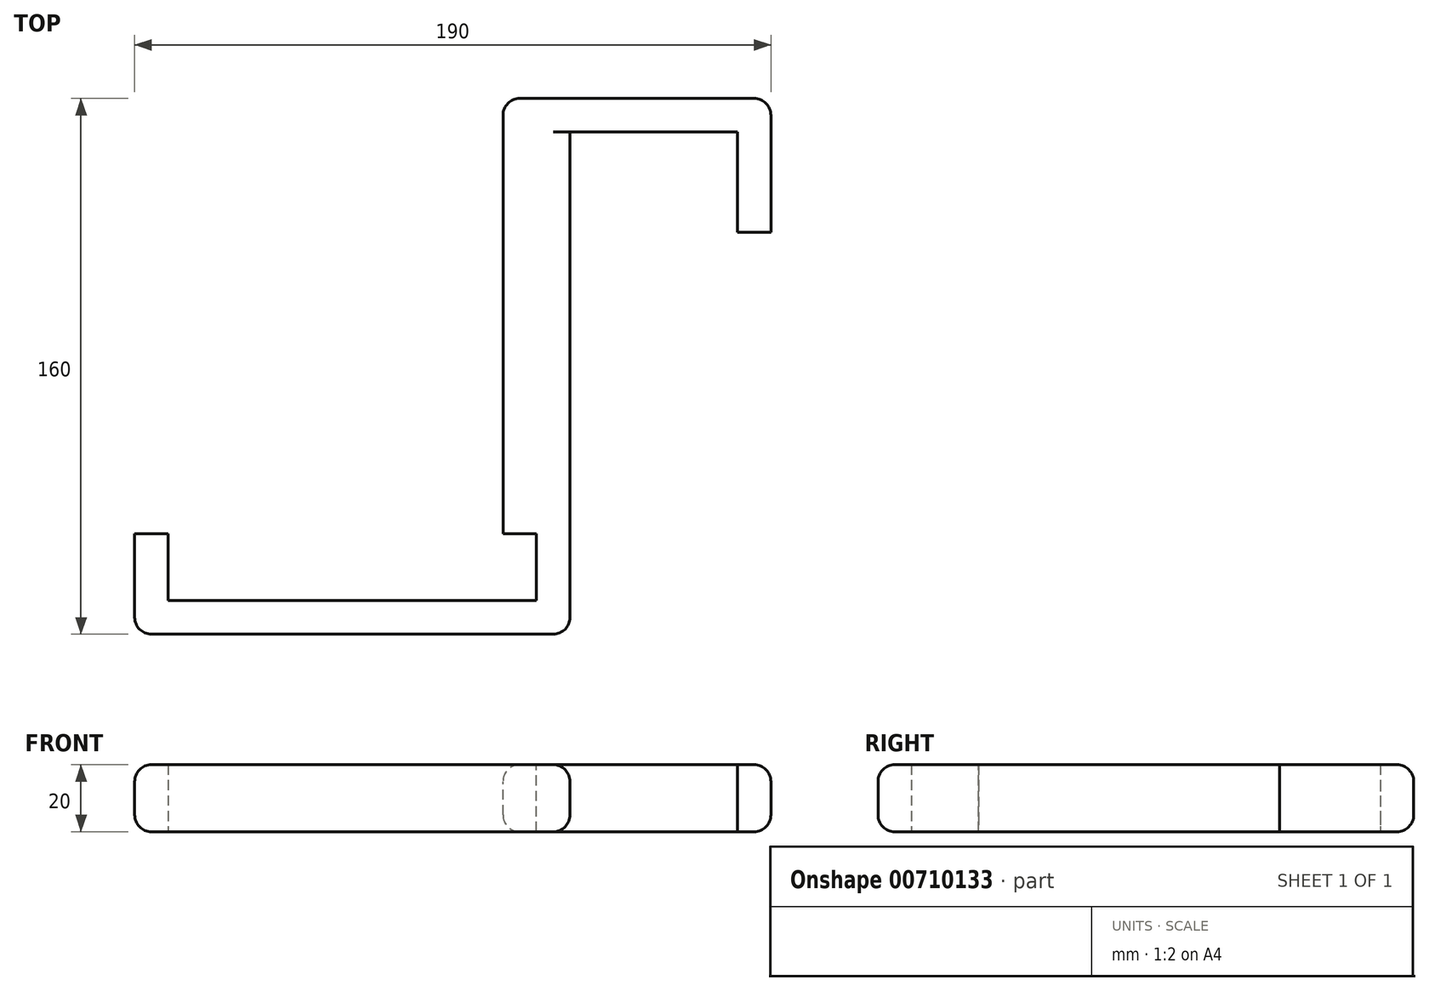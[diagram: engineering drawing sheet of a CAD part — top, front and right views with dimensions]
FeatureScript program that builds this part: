
annotation { "Feature Type Name" : "Feature", "Feature Type Description" : "" }
export const myFeature = defineFeature(function(context is Context, id is Id, definition is map)
    precondition{}
    {
        {
            var Q0;
            Q0=qCreatedBy(makeId("Top.planeOp"),FACE);
            var sketch = newSketch(context, id + "F0", { "sketchPlane" : qUnion([Q0])});
            skLineSegment(sketch, "E0.bottom", {"start": v(0, 0) * mm, "end": v(0, 0) * mm});
            skLineSegment(sketch, "E0.top", {"start": v(0, 0) * mm, "end": v(0, 0) * mm});
            skLineSegment(sketch, "E0.left", {"start": v(0, 0) * mm, "end": v(0, 0) * mm});
            skLineSegment(sketch, "E0.right", {"start": v(0, 0) * mm, "end": v(0, 0) * mm});
            skLineSegment(sketch, "E1.bottom", {"start": v(0, 0) * mm, "end": v(-110, 0) * mm});
            skLineSegment(sketch, "E1.top", {"start": v(0, -10) * mm, "end": v(-110, -10) * mm});
            skLineSegment(sketch, "E1.left", {"start": v(0, 0) * mm, "end": v(0, -10) * mm});
            skLineSegment(sketch, "E1.right", {"start": v(-110, 0) * mm, "end": v(-110, -10) * mm});
            skLineSegment(sketch, "E2.bottom", {"start": v(0, -10) * mm, "end": v(10, -10) * mm});
            skLineSegment(sketch, "E2.top", {"start": v(0, 140) * mm, "end": v(10, 140) * mm});
            skLineSegment(sketch, "E2.left", {"start": v(0, -10) * mm, "end": v(0, 140) * mm});
            skLineSegment(sketch, "E2.right", {"start": v(10, -10) * mm, "end": v(10, 140) * mm});
            skLineSegment(sketch, "E3.bottom", {"start": v(0, 140) * mm, "end": v(60, 140) * mm});
            skLineSegment(sketch, "E3.top", {"start": v(0, 150) * mm, "end": v(60, 150) * mm});
            skLineSegment(sketch, "E3.left", {"start": v(0, 140) * mm, "end": v(0, 150) * mm});
            skLineSegment(sketch, "E3.right", {"start": v(60, 140) * mm, "end": v(60, 150) * mm});
            skLineSegment(sketch, "E4.bottom", {"start": v(60, 150) * mm, "end": v(70, 150) * mm});
            skLineSegment(sketch, "E4.top", {"start": v(60, 110) * mm, "end": v(70, 110) * mm});
            skLineSegment(sketch, "E4.left", {"start": v(60, 150) * mm, "end": v(60, 110) * mm});
            skLineSegment(sketch, "E4.right", {"start": v(70, 150) * mm, "end": v(70, 110) * mm});
            skLineSegment(sketch, "E5.bottom", {"start": v(-110, -10) * mm, "end": v(-120, -10) * mm});
            skLineSegment(sketch, "E5.top", {"start": v(-110, 20) * mm, "end": v(-120, 20) * mm});
            skLineSegment(sketch, "E5.left", {"start": v(-110, -10) * mm, "end": v(-110, 20) * mm});
            skLineSegment(sketch, "E5.right", {"start": v(-120, -10) * mm, "end": v(-120, 20) * mm});
            skSolve(sketch);
        }
        {
            var Q0;
            {var subQ3=sQuery(id+"F0.wireOp",EDGE,"E4.bottom");Q0=makeQuery(id+"F0.imprint","IMPRINT",FACE,{"disambiguationData":[TD([[makeQuery(id+"F0.imprint","IMPRINT",EDGE,{"derivedFrom":subQ3}),-1.0]])]});}
            var Q1;
            {var subQ1=sQuery(id+"F0.wireOp",EDGE,"E3.top");Q1=makeQuery(id+"F0.imprint","IMPRINT",FACE,{"disambiguationData":[TD([[makeQuery(id+"F0.imprint","IMPRINT",EDGE,{"derivedFrom":subQ1}),-1.0]])]});}
            var Q2;
            {var subQ5=sQuery(id+"F0.wireOp",EDGE,"E2.bottom");Q2=makeQuery(id+"F0.imprint","IMPRINT",FACE,{"disambiguationData":[TD([[makeQuery(id+"F0.imprint","IMPRINT",EDGE,{"derivedFrom":subQ5}),1.0]])]});}
            var Q3;
            {var subQ0=sQuery(id+"F0.wireOp",EDGE,"E1.bottom");Q3=makeQuery(id+"F0.imprint","IMPRINT",FACE,{"disambiguationData":[TD([[makeQuery(id+"F0.imprint","IMPRINT",EDGE,{"derivedFrom":subQ0}),1.0]])]});}
            var Q4;
            {var subQ3=sQuery(id+"F0.wireOp",EDGE,"E5.bottom");Q4=makeQuery(id+"F0.imprint","IMPRINT",FACE,{"disambiguationData":[TD([[makeQuery(id+"F0.imprint","IMPRINT",EDGE,{"derivedFrom":subQ3}),-1.0]])]});}
            extrude(context, id + "F1", {"entities" : qUnion([Q0, Q1, Q2, Q3, Q4]), "depth" : 20 * mm, "offsetDistance" : 25 * mm});
        }
        {
            var Q0;
            Q0=makeQuery(id+"F1.opExtrude","SWEPT_FACE",FACE,{"disambiguationData":[OSD([sQuery(id+"F0.wireOp",EDGE,"E2.left"),sQuery(id+"F0.wireOp",EDGE,"E3.left")])]});
            var sketch = newSketch(context, id + "F2", { "sketchPlane" : qUnion([Q0])});
            skLineSegment(sketch, "E6", {"start": v(0, 0) * mm, "end": v(-20, 0) * mm});
            skLineSegment(sketch, "E7.top", {"start": v(0, 20) * mm, "end": v(-20, 20) * mm});
            skLineSegment(sketch, "E7.left", {"start": v(0, 0) * mm, "end": v(0, 20) * mm});
            skLineSegment(sketch, "E7.right", {"start": v(-20, 0) * mm, "end": v(-20, 20) * mm});
            skSolve(sketch);
        }
        {
            var Q0;
            {var subQ0=sQuery(id+"F2.wireOp",EDGE,"E7.right");Q0=makeQuery(id+"F2.imprint","IMPRINT",FACE,{"disambiguationData":[TD([[makeQuery(id+"F2.imprint","IMPRINT",EDGE,{"derivedFrom":subQ0}),1.0]])]});}
            extrude(context, id + "F3", {"entities" : qUnion([Q0]), "operationType" : NewBodyOperationType.ADD, "depth" : 10 * mm, "offsetDistance" : 25 * mm});
        }
        {
            var Q0;
            {var subQ0=sQuery(id+"F0.wireOp",EDGE,"E3.left");var subQ1=sQuery(id+"F0.wireOp",EDGE,"E2.left");var subQ2=sQuery(id+"F0.wireOp",EDGE,"E3.top");Q0=makeQuery(id+"F3.boolean.opBoolean","MERGE",EDGE,{"derivedFrom":[makeQuery(id+"F1.opExtrude","CAP_EDGE",EDGE,{"disambiguationData":[OSD([subQ2,sQuery(id+"F0.wireOp",EDGE,"E4.bottom")])],"isStart":false}),makeQuery(id+"F3.opExtrude","SWEPT_EDGE",EDGE,{"disambiguationData":[OSD([subQ1,subQ2,subQ0]),TDD([makeQuery(id+"F2.imprint","INTERSECT",VERTEX,{"derivedFrom":[makeQuery(id+"F1.opExtrude","SWEPT_EDGE",EDGE,{"disambiguationData":[OSD([subQ2,subQ0])]}),makeQuery(id+"F1.opExtrude","CAP_EDGE",EDGE,{"disambiguationData":[OSD([subQ1,subQ0])],"isStart":false})]})])]})]});}
            var Q1;
            {var subQ0=sQuery(id+"F0.wireOp",EDGE,"E3.left");var subQ1=sQuery(id+"F0.wireOp",EDGE,"E2.left");var subQ2=sQuery(id+"F0.wireOp",EDGE,"E3.top");Q1=makeQuery(id+"F3.boolean.opBoolean","MERGE",EDGE,{"derivedFrom":[makeQuery(id+"F1.opExtrude","CAP_EDGE",EDGE,{"disambiguationData":[OSD([subQ2,sQuery(id+"F0.wireOp",EDGE,"E4.bottom")])],"isStart":true}),makeQuery(id+"F3.opExtrude","SWEPT_EDGE",EDGE,{"disambiguationData":[OSD([subQ1,subQ2,subQ0]),TDD([makeQuery(id+"F2.imprint","INTERSECT",VERTEX,{"derivedFrom":[makeQuery(id+"F1.opExtrude","SWEPT_EDGE",EDGE,{"disambiguationData":[OSD([subQ2,subQ0])]}),makeQuery(id+"F1.opExtrude","CAP_EDGE",EDGE,{"disambiguationData":[OSD([subQ1,subQ0])],"isStart":true})]})])]})]});}
            var Q2;
            Q2=makeQuery(id+"F1.opExtrude","CAP_EDGE",EDGE,{"disambiguationData":[OSD([sQuery(id+"F0.wireOp",EDGE,"E4.right")])],"isStart":true});
            var Q3;
            Q3=makeQuery(id+"F1.opExtrude","CAP_EDGE",EDGE,{"disambiguationData":[OSD([sQuery(id+"F0.wireOp",EDGE,"E4.right")])],"isStart":false});
            var Q4;
            Q4=makeQuery(id+"F1.opExtrude","SWEPT_EDGE",EDGE,{"disambiguationData":[OSD([sQuery(id+"F0.wireOp",EDGE,"E4.bottom"),sQuery(id+"F0.wireOp",EDGE,"E4.right")])]});
            var Q5;
            Q5=makeQuery(id+"F3.opExtrude","CAP_EDGE",EDGE,{"disambiguationData":[OSD([sQuery(id+"F0.wireOp",EDGE,"E3.top"),sQuery(id+"F0.wireOp",EDGE,"E3.left")])],"isStart":false});
            var Q6;
            {var subQ0=sQuery(id+"F0.wireOp",EDGE,"E3.left");var subQ1=sQuery(id+"F0.wireOp",EDGE,"E2.left");var subQ2=makeQuery(id+"F1.opExtrude","CAP_EDGE",EDGE,{"disambiguationData":[OSD([subQ1,subQ0])],"isStart":false});Q6=makeQuery(id+"F3.opExtrude","CAP_EDGE",EDGE,{"disambiguationData":[OSD([subQ1,subQ0]),TDD([makeQuery(id+"F2.imprint","IMPRINT",EDGE,{"disambiguationData":[TD([[makeQuery(id+"F2.imprint","INTERSECT",VERTEX,{"derivedFrom":[makeQuery(id+"F1.opExtrude","SWEPT_EDGE",EDGE,{"disambiguationData":[OSD([sQuery(id+"F0.wireOp",EDGE,"E3.top"),subQ0])]}),subQ2]}),1.0]])],"derivedFrom":subQ2})])],"isStart":false});}
            var Q7;
            {var subQ0=sQuery(id+"F0.wireOp",EDGE,"E3.left");var subQ1=sQuery(id+"F0.wireOp",EDGE,"E2.left");var subQ2=makeQuery(id+"F1.opExtrude","CAP_EDGE",EDGE,{"disambiguationData":[OSD([subQ1,subQ0])],"isStart":true});Q7=makeQuery(id+"F3.opExtrude","CAP_EDGE",EDGE,{"disambiguationData":[OSD([subQ1,subQ0]),TDD([makeQuery(id+"F2.imprint","IMPRINT",EDGE,{"disambiguationData":[TD([[makeQuery(id+"F2.imprint","INTERSECT",VERTEX,{"derivedFrom":[makeQuery(id+"F1.opExtrude","SWEPT_EDGE",EDGE,{"disambiguationData":[OSD([sQuery(id+"F0.wireOp",EDGE,"E3.top"),subQ0])]}),subQ2]}),1.0]])],"derivedFrom":subQ2})])],"isStart":false});}
            var Q8;
            Q8=makeQuery(id+"F1.opExtrude","CAP_EDGE",EDGE,{"disambiguationData":[OSD([sQuery(id+"F0.wireOp",EDGE,"E1.top"),sQuery(id+"F0.wireOp",EDGE,"E2.bottom")])],"isStart":false});
            var Q9;
            Q9=makeQuery(id+"F1.opExtrude","SWEPT_EDGE",EDGE,{"disambiguationData":[OSD([sQuery(id+"F0.wireOp",EDGE,"E2.bottom"),sQuery(id+"F0.wireOp",EDGE,"E2.right")])]});
            var Q10;
            Q10=makeQuery(id+"F1.opExtrude","CAP_EDGE",EDGE,{"disambiguationData":[OSD([sQuery(id+"F0.wireOp",EDGE,"E2.right")])],"isStart":true});
            var Q11;
            Q11=makeQuery(id+"F1.opExtrude","CAP_EDGE",EDGE,{"disambiguationData":[OSD([sQuery(id+"F0.wireOp",EDGE,"E2.right")])],"isStart":false});
            var Q12;
            Q12=makeQuery(id+"F1.opExtrude","CAP_EDGE",EDGE,{"disambiguationData":[OSD([sQuery(id+"F0.wireOp",EDGE,"E5.right")])],"isStart":false});
            var Q13;
            Q13=makeQuery(id+"F1.opExtrude","CAP_EDGE",EDGE,{"disambiguationData":[OSD([sQuery(id+"F0.wireOp",EDGE,"E5.right")])],"isStart":true});
            var Q14;
            Q14=makeQuery(id+"F1.opExtrude","SWEPT_EDGE",EDGE,{"disambiguationData":[OSD([sQuery(id+"F0.wireOp",EDGE,"E5.bottom"),sQuery(id+"F0.wireOp",EDGE,"E5.right")])]});
            var Q15;
            Q15=makeQuery(id+"F1.opExtrude","CAP_EDGE",EDGE,{"disambiguationData":[OSD([sQuery(id+"F0.wireOp",EDGE,"E1.top"),sQuery(id+"F0.wireOp",EDGE,"E2.bottom"),sQuery(id+"F0.wireOp",EDGE,"E5.bottom")])],"isStart":true});
            fillet(context, id + "F4", {"entities" : qUnion([Q0, Q1, Q2, Q3, Q4, Q5, Q6, Q7, Q8, Q9, Q10, Q11, Q12, Q13, Q14, Q15]), "radius" : 5 * mm, "allowEdgeOverflow" : false});
        }
    });
